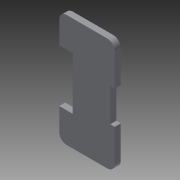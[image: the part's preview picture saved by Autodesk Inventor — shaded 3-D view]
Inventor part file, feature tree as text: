
AUTODESK INVENTOR PART (.ipt)
format: ipt  version: 2015 (Build 190159000, 159)  size: 92,672 bytes
history: native  units: mm
features: extrude x1, sketch x1
ambient origin geometry x8: Origin, YZ Plane, XZ Plane, XY Plane, X Axis, Y Axis, Z Axis, Center Point
bodies: Solid1 (feature_tree)
feature tree (2):
  extrude  "Extrusion1"  Depth=150.0mm
  sketch  "Sketch1"  dims[d0=74.0mm d1=150.0mm d2=53.0mm d3=6.0mm d4=44.0mm d5=40.0mm d6=18.0mm d7=70.0mm d8=10.0mm d9=8.0mm d10=0.0mm]
